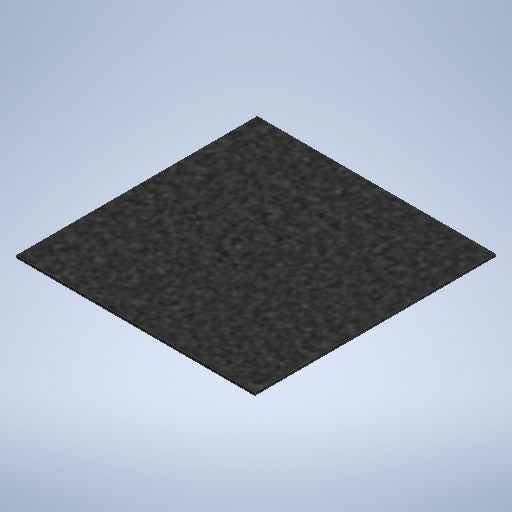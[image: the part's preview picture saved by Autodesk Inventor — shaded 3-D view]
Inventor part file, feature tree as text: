
AUTODESK INVENTOR PART (.ipt)
format: ipt  version: 2025.1 (Build 291241020, 241B)  size: 281,088 bytes
history: native  units: in
note: dims shown in document units (in); Inventor stores cm internally (conversion verified against a paired STEP export)
features: extrude x1, sketch x1
ambient origin geometry x8: Origin, YZ Plane, XZ Plane, XY Plane, X Axis, Y Axis, Z Axis, Center Point
bodies: Solid1 (feature_tree)
feature tree (2):
  extrude  "Extrusion1"  Depth=0.125in TaperAngle=0.0deg
  sketch  "Sketch1"  dims[d1=12.0in d2=0.125in d3=0.0in d4=12.125in]
